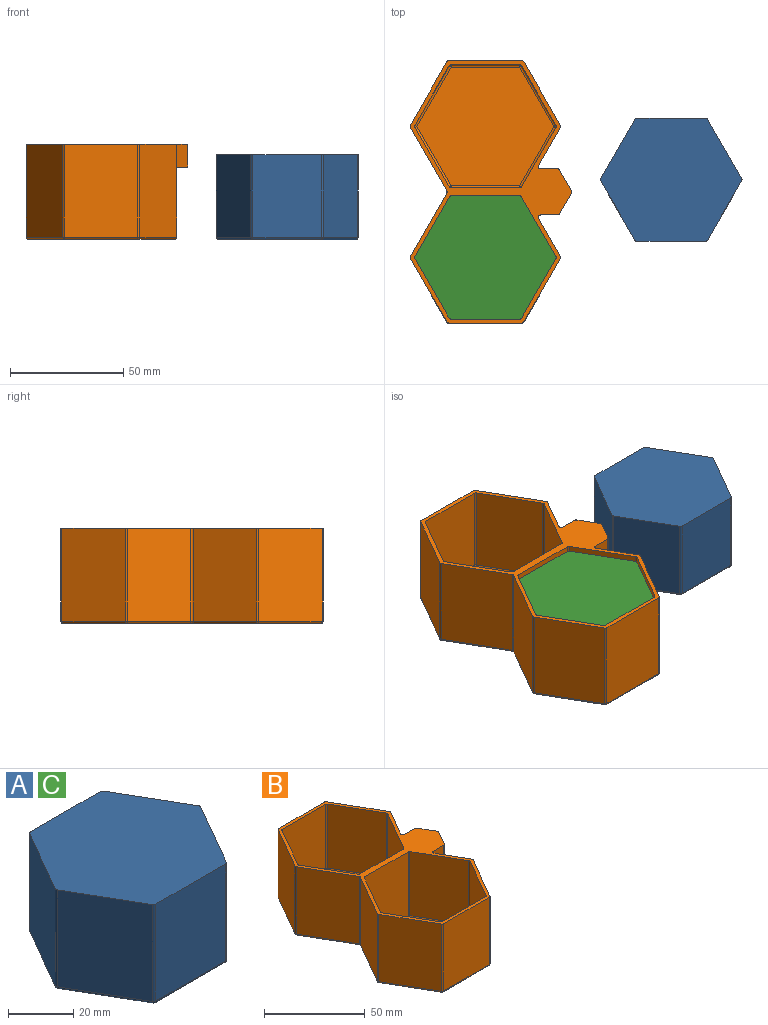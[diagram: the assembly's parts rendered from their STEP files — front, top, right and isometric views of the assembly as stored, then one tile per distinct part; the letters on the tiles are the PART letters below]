
ASSEMBLY  parts=3 mates=1
PART A: 26 faces, bbox 62.6x54.5x37.5 mm
  f0: plane 36.5x30.31mm, normal (0,-1,0), area 1106.3mm2, adj f6,f19,f23,f25
  f1: plane 36.5x26.25mm, normal (0.87,-0.5,0), area 1106.3mm2, adj f6,f16,f22,f25
  f2: plane 36.5x26.25mm, normal (0.87,0.5,0), area 1106.3mm2, adj f6,f10,f16,f17
  f3: plane 36.5x30.31mm, normal (0,1,0), area 1106.3mm2, adj f6,f8,f10,f11
  f4: plane 36.5x26.25mm, normal (-0.87,0.5,0), area 1106.3mm2, adj f6,f8,f12,f13
  f5: plane 36.5x26.25mm, normal (-0.87,-0.5,0), area 1106.3mm2, adj f6,f13,f18,f19
  f6: plane 62.62x54.5mm, normal (0,0,1), area 2572mm2, adj f0,f1,f2,f3,f4,f5,f8,f10
  f7: plane 60.62x52.5mm, normal (0,0,-1), area 2387mm2, adj f11,f12,f17,f18,f22,f23
  f8: cylinder r=1mm len=36.5mm, axis (0,0,-1), area 38.2mm2, adj f3,f4,f6,f9
  f9: sphere r=1mm, area 1mm2, adj f8,f11,f12
  f10: cylinder r=1mm len=36.5mm, axis (0,0,-1), area 38.2mm2, adj f2,f3,f6,f14
  f11: cylinder r=1mm len=30.31mm, axis (-1,0,0), area 47.6mm2, adj f3,f7,f9,f14
  f12: cylinder r=1mm len=26.75mm, axis (-0.5,-0.87,0), area 47.6mm2, adj f4,f7,f9,f15
  f13: cylinder r=1mm len=36.5mm, axis (0,0,-1), area 38.2mm2, adj f4,f5,f6,f15
  f14: sphere r=1mm, area 1mm2, adj f10,f11,f17
  f15: sphere r=1mm, area 1mm2, adj f12,f13,f18
  f16: cylinder r=1mm len=36.5mm, axis (0,0,-1), area 38.2mm2, adj f1,f2,f6,f20
  f17: cylinder r=1mm len=26.75mm, axis (-0.5,0.87,0), area 47.6mm2, adj f2,f7,f14,f20
  f18: cylinder r=1mm len=26.75mm, axis (0.5,-0.87,0), area 47.6mm2, adj f5,f7,f15,f21
  f19: cylinder r=1mm len=36.5mm, axis (0,0,-1), area 38.2mm2, adj f0,f5,f6,f21
  f20: sphere r=1mm, area 1mm2, adj f16,f17,f22
  f21: sphere r=1mm, area 1mm2, adj f18,f19,f23
  f22: cylinder r=1mm len=26.75mm, axis (0.5,0.87,0), area 47.6mm2, adj f1,f7,f20,f24
  f23: cylinder r=1mm len=30.31mm, axis (1,0,0), area 47.6mm2, adj f0,f7,f21,f24
  f24: sphere r=1mm, area 1mm2, adj f22,f23,f25
  f25: cylinder r=1mm len=36.5mm, axis (0,0,-1), area 38.2mm2, adj f0,f1,f6,f24
PART B: 117 faces, bbox 71.5x116x42 mm
  f0: plane 23.37x16.46mm, normal (0,0,-1), area 63.5mm2, adj f1,f2,f27,f28,f29,f30,f42,f43
  f1: plane 41x28mm, normal (0.87,0.5,0), area 1196.4mm2, adj f0,f3,f32,f46,f89,f95,f96
  f2: plane 41x28mm, normal (0.87,-0.5,0), area 1196.4mm2, adj f0,f3,f32,f47,f87,f89,f90
  f3: plane 116x71.55mm, normal (0,0,1), area 1004.2mm2, adj f1,f2,f4,f5,f6,f7,f8,f9
  f4: plane 41x28mm, normal (-0.87,0.5,0), area 1325.6mm2, adj f3,f110,f114,f116
  f5: plane 41x28mm, normal (-0.87,-0.5,0), area 1325.6mm2, adj f3,f107,f113,f116
  f6: plane 41x32.33mm, normal (0,-1,0), area 1325.6mm2, adj f3,f101,f107,f108
  f7: plane 41x28mm, normal (0.87,-0.5,0), area 1325.6mm2, adj f3,f95,f101,f102
  f8: plane 41x28mm, normal (0.87,0.5,0), area 1325.6mm2, adj f3,f87,f91,f92
  f9: plane 41x32.33mm, normal (0,1,0), area 1325.6mm2, adj f3,f92,f97,f98
  f10: plane 41x28mm, normal (-0.87,0.5,0), area 1325.6mm2, adj f3,f98,f103,f104
  f11: plane 41x28mm, normal (-0.87,-0.5,0), area 1325.6mm2, adj f3,f104,f109,f110
  f12: plane 114x64.66mm, normal (0,0,-1), area 5495.6mm2, adj f90,f91,f93,f96,f97,f102,f103,f108
  f13: plane 39x30.31mm, normal (0,1,0), area 1182.1mm2, adj f3,f59,f65,f68
  f14: plane 39x26.25mm, normal (-0.87,0.5,0), area 1182.1mm2, adj f3,f62,f66,f68
  f15: plane 39x26.25mm, normal (-0.87,-0.5,0), area 1182.1mm2, adj f3,f56,f61,f62
  f16: plane 39x30.31mm, normal (0,-1,0), area 1182.1mm2, adj f3,f51,f55,f56
  f17: plane 39x26.25mm, normal (0.87,-0.5,0), area 1182.1mm2, adj f3,f51,f53,f54
  f18: plane 39x26.25mm, normal (0.87,0.5,0), area 1182.1mm2, adj f3,f53,f59,f60
  f19: plane 60.62x52.5mm, normal (0,0,1), area 2387mm2, adj f54,f55,f60,f61,f65,f66
  f20: plane 39x26.25mm, normal (0.87,-0.5,0), area 1182.1mm2, adj f3,f80,f84,f86
  f21: plane 39x26.25mm, normal (0.87,0.5,0), area 1182.1mm2, adj f3,f74,f79,f80
  f22: plane 39x30.31mm, normal (0,1,0), area 1182.1mm2, adj f3,f69,f73,f74
  f23: plane 39x26.25mm, normal (-0.87,0.5,0), area 1182.1mm2, adj f3,f69,f71,f72
  f24: plane 39x26.25mm, normal (-0.87,-0.5,0), area 1182.1mm2, adj f3,f71,f77,f78
  f25: plane 39x30.31mm, normal (0,-1,0), area 1182.1mm2, adj f3,f77,f83,f86
  f26: plane 60.62x52.5mm, normal (0,0,1), area 2387mm2, adj f72,f73,f78,f79,f83,f84
  f27: plane 10x7.56mm, normal (0,-1,0), area 75.5mm2, adj f0,f3,f46,f48
  f28: plane 10x9.19mm, normal (0.87,-0.5,0), area 106.1mm2, adj f0,f3,f48,f49
  f29: plane 10x9.19mm, normal (0.87,0.5,0), area 106.1mm2, adj f0,f3,f49,f50
  f30: plane 10x7.56mm, normal (0,1,0), area 75.5mm2, adj f0,f3,f47,f50
  f31: plane 30.5x0.25mm, normal (-0.87,0.5,0), area 8.8mm2, adj f32,f33,f34,f38
  f32: plane 17.37x6.75mm, normal (0,0,1), area 5.8mm2, adj f1,f2,f31,f34,f38,f39,f40,f41
  f33: plane 30.31x0.5mm, normal (0,0,1), area 15.1mm2, adj f31,f34,f36,f37,f38,f41
  f34: plane 30.5x0.25mm, normal (-0.87,-0.5,0), area 8.8mm2, adj f31,f32,f33,f41
  f35: plane 51.79x17.37mm, normal (0,0,-1), area 279.3mm2, adj f36,f37,f38,f39,f40,f41,f42,f43
  f36: plane 39x0.25mm, normal (0.87,-0.5,0), area 11.3mm2, adj f33,f35,f37,f41
  f37: plane 39x0.25mm, normal (0.87,0.5,0), area 11.3mm2, adj f33,f35,f36,f38
  f38: plane 39x31.75mm, normal (0,-1,0), area 1194.4mm2, adj f31,f32,f33,f35,f37,f39
  f39: plane 8.5x8.44mm, normal (0.87,-0.5,0), area 82.8mm2, adj f32,f35,f38,f45
  f40: plane 8.5x8.44mm, normal (0.87,0.5,0), area 82.8mm2, adj f32,f35,f41,f42
  f41: plane 39x31.75mm, normal (0,1,0), area 1194.4mm2, adj f32,f33,f34,f35,f36,f40
  f42: plane 10.15x8.5mm, normal (0,1,0), area 86.3mm2, adj f0,f32,f35,f40,f43
  f43: plane 8.69x8.5mm, normal (-0.87,0.5,0), area 85.2mm2, adj f0,f35,f42,f44
  f44: plane 8.69x8.5mm, normal (-0.87,-0.5,0), area 85.2mm2, adj f0,f35,f43,f45
  f45: plane 10.15x8.5mm, normal (0,-1,0), area 86.3mm2, adj f0,f32,f35,f39,f44
  f46: cylinder r=1mm len=10mm, axis (0,0,1), area 20.9mm2, adj f0,f1,f3,f27
  f47: cylinder r=1mm len=10mm, axis (0,0,-1), area 20.9mm2, adj f0,f2,f3,f30
  f48: cylinder r=1mm len=10mm, axis (0,0,1), area 10.5mm2, adj f0,f3,f27,f28
  f49: cylinder r=1mm len=10mm, axis (0,0,1), area 10.5mm2, adj f0,f3,f28,f29
  f50: cylinder r=1mm len=10mm, axis (0,0,1), area 10.5mm2, adj f0,f3,f29,f30
  f51: cylinder r=1mm len=39mm, axis (0,0,-1), area 40.8mm2, adj f3,f16,f17,f52
  f52: sphere r=1mm, area 1mm2, adj f51,f54,f55
  f53: cylinder r=1mm len=39mm, axis (0,0,-1), area 40.8mm2, adj f3,f17,f18,f57
  f54: cylinder r=1mm len=26.75mm, axis (-0.5,-0.87,0), area 47.6mm2, adj f17,f19,f52,f57
  f55: cylinder r=1mm len=30.31mm, axis (-1,0,0), area 47.6mm2, adj f16,f19,f52,f58
  f56: cylinder r=1mm len=39mm, axis (0,0,-1), area 40.8mm2, adj f3,f15,f16,f58
  f57: sphere r=1mm, area 1mm2, adj f53,f54,f60
  f58: sphere r=1mm, area 1mm2, adj f55,f56,f61
  f59: cylinder r=1mm len=39mm, axis (0,0,-1), area 40.8mm2, adj f3,f13,f18,f63
  f60: cylinder r=1mm len=26.75mm, axis (0.5,-0.87,0), area 47.6mm2, adj f18,f19,f57,f63
  f61: cylinder r=1mm len=26.75mm, axis (-0.5,0.87,0), area 47.6mm2, adj f15,f19,f58,f64
  f62: cylinder r=1mm len=39mm, axis (0,0,-1), area 40.8mm2, adj f3,f14,f15,f64
  f63: sphere r=1mm, area 1mm2, adj f59,f60,f65
  f64: sphere r=1mm, area 1mm2, adj f61,f62,f66
  f65: cylinder r=1mm len=30.31mm, axis (1,0,0), area 47.6mm2, adj f13,f19,f63,f67
  f66: cylinder r=1mm len=26.75mm, axis (0.5,0.87,0), area 47.6mm2, adj f14,f19,f64,f67
  f67: sphere r=1mm, area 1mm2, adj f65,f66,f68
  f68: cylinder r=1mm len=39mm, axis (0,0,-1), area 40.8mm2, adj f3,f13,f14,f67
  f69: cylinder r=1mm len=39mm, axis (0,0,-1), area 40.8mm2, adj f3,f22,f23,f70
  f70: sphere r=1mm, area 1mm2, adj f69,f72,f73
  f71: cylinder r=1mm len=39mm, axis (0,0,-1), area 40.8mm2, adj f3,f23,f24,f75
  f72: cylinder r=1mm len=26.75mm, axis (0.5,0.87,0), area 47.6mm2, adj f23,f26,f70,f75
  f73: cylinder r=1mm len=30.31mm, axis (1,0,0), area 47.6mm2, adj f22,f26,f70,f76
  f74: cylinder r=1mm len=39mm, axis (0,0,-1), area 40.8mm2, adj f3,f21,f22,f76
  f75: sphere r=1mm, area 1mm2, adj f71,f72,f78
  f76: sphere r=1mm, area 1mm2, adj f73,f74,f79
  f77: cylinder r=1mm len=39mm, axis (0,0,-1), area 40.8mm2, adj f3,f24,f25,f81
  f78: cylinder r=1mm len=26.75mm, axis (-0.5,0.87,0), area 47.6mm2, adj f24,f26,f75,f81
  f79: cylinder r=1mm len=26.75mm, axis (0.5,-0.87,0), area 47.6mm2, adj f21,f26,f76,f82
  f80: cylinder r=1mm len=39mm, axis (0,0,-1), area 40.8mm2, adj f3,f20,f21,f82
  f81: sphere r=1mm, area 1mm2, adj f77,f78,f83
  f82: sphere r=1mm, area 1mm2, adj f79,f80,f84
  f83: cylinder r=1mm len=30.31mm, axis (-1,0,0), area 47.6mm2, adj f25,f26,f81,f85
  f84: cylinder r=1mm len=26.75mm, axis (-0.5,-0.87,0), area 47.6mm2, adj f20,f26,f82,f85
  f85: sphere r=1mm, area 1mm2, adj f83,f84,f86
  f86: cylinder r=1mm len=39mm, axis (0,0,-1), area 40.8mm2, adj f3,f20,f25,f85
  f87: cylinder r=1mm len=41mm, axis (0,0,-1), area 42.9mm2, adj f2,f3,f8,f88
  f88: sphere r=1mm, area 1mm2, adj f87,f90,f91
  f89: cylinder r=1mm len=31mm, axis (0,0,1), area 32.5mm2, adj f1,f2,f32,f93
  f90: cylinder r=1mm len=28.5mm, axis (0.5,0.87,0), area 50.8mm2, adj f2,f12,f88,f93
  f91: cylinder r=1mm len=28.5mm, axis (-0.5,0.87,0), area 50.8mm2, adj f8,f12,f88,f94
  f92: cylinder r=1mm len=41mm, axis (0,0,-1), area 42.9mm2, adj f3,f8,f9,f94
  f93: torus R=2mm, axis (0,0,1), area 2.2mm2, adj f12,f89,f90,f96
  f94: sphere r=1mm, area 1mm2, adj f91,f92,f97
  f95: cylinder r=1mm len=41mm, axis (0,0,-1), area 42.9mm2, adj f1,f3,f7,f99
  f96: cylinder r=1mm len=28.5mm, axis (-0.5,0.87,0), area 50.8mm2, adj f1,f12,f93,f99
  f97: cylinder r=1mm len=32.33mm, axis (-1,0,0), area 50.8mm2, adj f9,f12,f94,f100
  f98: cylinder r=1mm len=41mm, axis (0,0,-1), area 42.9mm2, adj f3,f9,f10,f100
  f99: sphere r=1mm, area 1mm2, adj f95,f96,f102
  f100: sphere r=1mm, area 1mm2, adj f97,f98,f103
  f101: cylinder r=1mm len=41mm, axis (0,0,-1), area 42.9mm2, adj f3,f6,f7,f105
  f102: cylinder r=1mm len=28.5mm, axis (0.5,0.87,0), area 50.8mm2, adj f7,f12,f99,f105
  f103: cylinder r=1mm len=28.5mm, axis (-0.5,-0.87,0), area 50.8mm2, adj f10,f12,f100,f106
  f104: cylinder r=1mm len=41mm, axis (0,0,-1), area 42.9mm2, adj f3,f10,f11,f106
  f105: sphere r=1mm, area 1mm2, adj f101,f102,f108
  f106: sphere r=1mm, area 1mm2, adj f103,f104,f109
  f107: cylinder r=1mm len=41mm, axis (0,0,-1), area 42.9mm2, adj f3,f5,f6,f111
  f108: cylinder r=1mm len=32.33mm, axis (1,0,0), area 50.8mm2, adj f6,f12,f105,f111
  f109: cylinder r=1mm len=28.5mm, axis (0.5,-0.87,0), area 50.8mm2, adj f11,f12,f106,f112
  f110: cylinder r=1mm len=41mm, axis (0,0,1), area 42.9mm2, adj f3,f4,f11,f112
  f111: sphere r=1mm, area 1mm2, adj f107,f108,f113
  f112: torus R=2mm, axis (0,0,1), area 2.2mm2, adj f12,f109,f110,f114
  f113: cylinder r=1mm len=28.5mm, axis (0.5,-0.87,0), area 50.8mm2, adj f5,f12,f111,f115
  f114: cylinder r=1mm len=28.5mm, axis (-0.5,-0.87,0), area 50.8mm2, adj f4,f12,f112,f115
  f115: sphere r=1mm, area 1mm2, adj f113,f114,f116
  f116: cylinder r=1mm len=41mm, axis (0,0,-1), area 42.9mm2, adj f3,f4,f5,f115
PART C: same geometry as A
PLACE A t=(138.14,27.79,18.97)mm
PLACE B t=(56,22.36,19.05)mm
PLACE C t=(56,-6.64,21.05)mm
MATE planar C.f7 <-> B.f26  axis (0,0,-1) through (56,-6.64,21.05)mm
